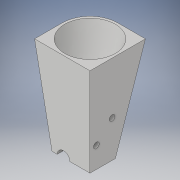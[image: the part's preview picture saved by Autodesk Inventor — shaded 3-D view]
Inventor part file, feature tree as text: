
AUTODESK INVENTOR PART (.ipt)
format: ipt  version: 2018 (Build 220112000, 112)  size: 185,856 bytes
history: native  units: in
note: dims shown in document units (in); Inventor stores cm internally (conversion verified against a paired STEP export)
features: sketch x6, loft x2, extrude x2, plane x1
ambient origin geometry x8: Origin, YZ Plane, XZ Plane, XY Plane, X Axis, Y Axis, Z Axis, Center Point
bodies: Solid1 (feature_tree)
feature tree (11):
  sketch  "Sketch1"  dims[d1=0.8in d2=1.2in]
  plane  "Work Plane1"
  loft  "Loft1"
  loft  "Loft2"
  extrude  "Extrusion1"  Depth=0.875in
  extrude  "Extrusion3"  TaperAngle=0.0deg  [1 undecoded]
  sketch  "Sketch3"  dims[d4=0.4in d5=2.8in]
  sketch  "Sketch4"  dims[d15=0.875in d17=0.875in]
  sketch  "Sketch5"  dims[d18=0.875in d19=0.0in d20=90.0deg]
  sketch  "Sketch6"  dims[d21=0.0in d22=90.0deg]
  sketch  "Sketch8"  dims[d23=1.6in d24=0.875in d26=0.875in d27=0.65in d28=0.0in d29=90.0deg d30=0.0in d31=90.0deg d32=0.4in d33=0.4in d34=0.4in d35=0.2in d36=0.0in d38=3.0in d39=0.0in d42=0.0in d43=0.25in d44=0.32in d45=0.09in d46=0.18in d47=0.2in d48=0.18in d49=0.5in d50=0.5in d51=1.0in d52=0.0in]
note: 1 required parameter value undecoded (feature->parameter linkage not recoverable at this tier; creation-order binding heuristic only, values carry confidence <= 0.55)
